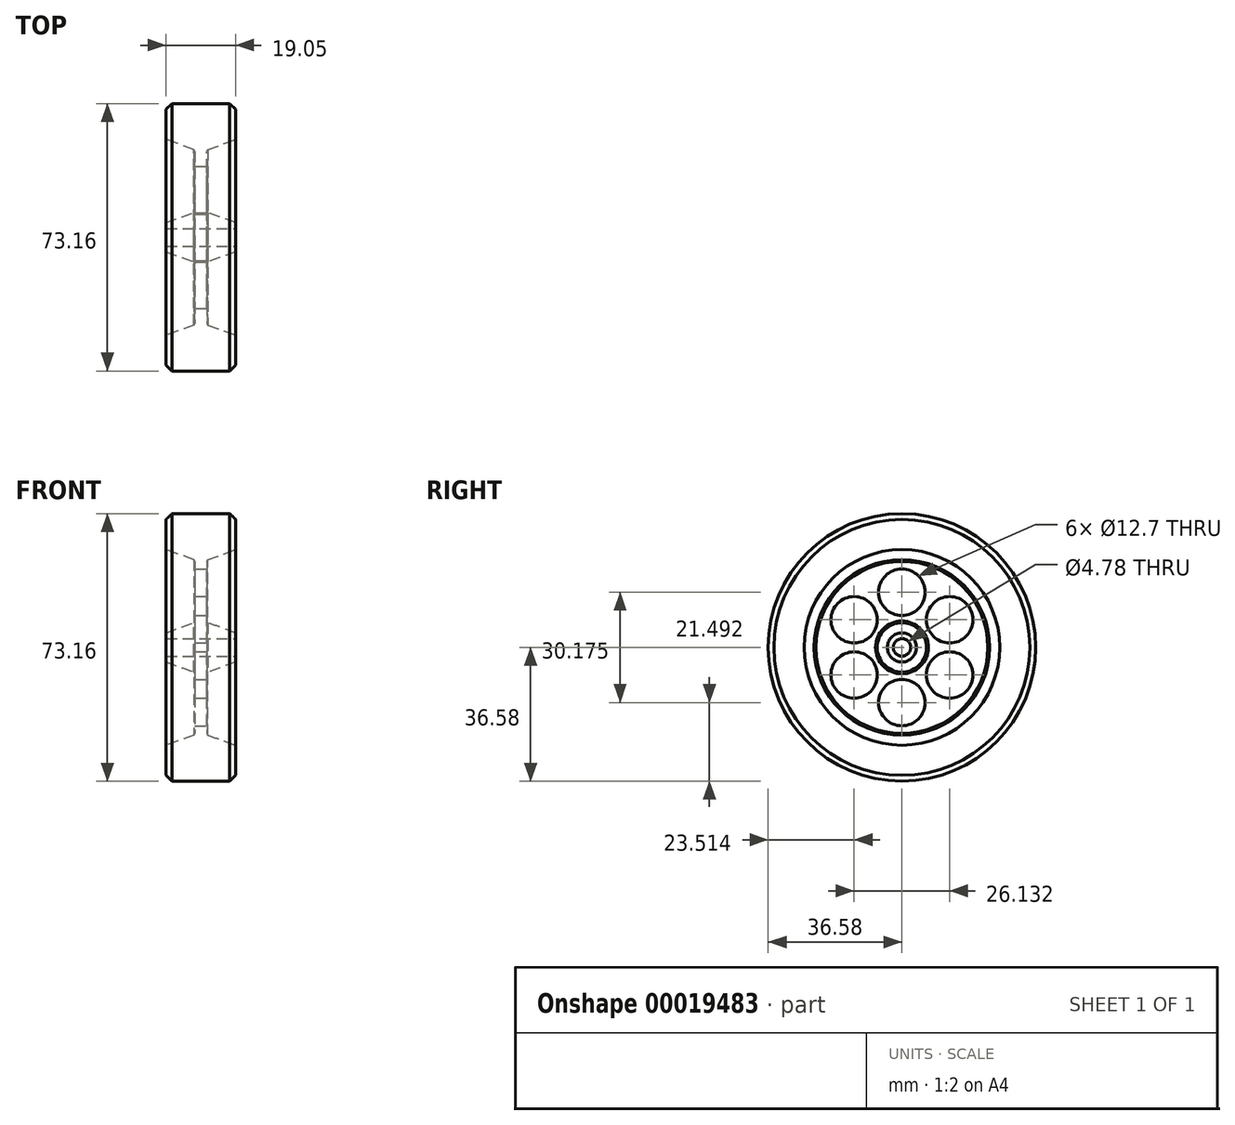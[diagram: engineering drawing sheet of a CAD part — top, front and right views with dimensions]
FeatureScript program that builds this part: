
annotation { "Feature Type Name" : "Feature", "Feature Type Description" : "" }
export const myFeature = defineFeature(function(context is Context, id is Id, definition is map)
    precondition{}
    {
        {
            var Q0;
            Q0=qCreatedBy(makeId("Front.planeOp"),FACE);
            var sketch = newSketch(context, id + "F0", { "sketchPlane" : qUnion([Q0])});
            skLineSegment(sketch, "E0", {"start": v(0, 0) * mm, "end": v(0, -3.98) * mm});
            skLineSegment(sketch, "E1", {"start": v(0, -3.98) * mm, "end": v(7.92, -6.86) * mm});
            skLineSegment(sketch, "E2", {"start": v(7.92, -6.86) * mm, "end": v(7.92, -23.88) * mm});
            skLineSegment(sketch, "E3", {"start": v(7.92, -23.88) * mm, "end": v(0, -26.76) * mm});
            skLineSegment(sketch, "E4", {"start": v(0, -26.76) * mm, "end": v(0, -36.58) * mm});
            skLineSegment(sketch, "E5", {"start": v(0, -36.58) * mm, "end": v(9.53, -36.58) * mm});
            skLineSegment(sketch, "E6", {"start": v(0, 0) * mm, "end": v(29.58, 0) * mm, "construction": true});
            skLineSegment(sketch, "E7", {"start": v(9.53, -36.58) * mm, "end": v(9.53, 2.67) * mm, "construction": true});
            skLineSegment(sketch, "E8.MirrorCS", {"start": v(11.13, -6.86) * mm, "end": v(11.13, -23.88) * mm});
            skLineSegment(sketch, "E9.MirrorCS", {"start": v(11.13, -23.88) * mm, "end": v(19.05, -26.76) * mm});
            skLineSegment(sketch, "E10.MirrorCS", {"start": v(19.05, -3.98) * mm, "end": v(11.13, -6.86) * mm});
            skLineSegment(sketch, "E11.MirrorCS", {"start": v(19.05, -26.76) * mm, "end": v(19.05, -36.58) * mm});
            skLineSegment(sketch, "E12.MirrorCS", {"start": v(19.05, -36.58) * mm, "end": v(9.53, -36.58) * mm});
            skLineSegment(sketch, "E13.MirrorCS", {"start": v(19.05, 0) * mm, "end": v(19.05, -3.98) * mm});
            skLineSegment(sketch, "E14", {"start": v(0, 0) * mm, "end": v(19.05, 0) * mm});
            skSolve(sketch);
        }
        {
            var Q0;
            Q0 = qSketchRegion(id + "F0", true);
            var Q1;
            Q1=sQuery(id+"F0.wireOp",EDGE,"E6");
            revolve(context, id + "F1", {"entities" : qUnion([Q0]), "axis" : qUnion([Q1]), "revolveType" : RevolveType.FULL});
        }
        {
            var Q0;
            Q0=makeQuery(id+"F1.opRevolve","SWEPT_FACE",FACE,{"disambiguationData":[OSD([sQuery(id+"F0.wireOp",EDGE,"E8.MirrorCS")])]});
            var sketch = newSketch(context, id + "F2", { "sketchPlane" : qUnion([Q0])});
            skCircle(sketch, "E15", {"center": v(0, 15.09) * mm, "radius": 6.35 * mm});
            skCircle(sketch, "E16.1.0", {"center": v(-13.07, 7.54) * mm, "radius": 6.35 * mm});
            skCircle(sketch, "E16.2.0", {"center": v(-13.07, -7.54) * mm, "radius": 6.35 * mm});
            skCircle(sketch, "E16.3.0", {"center": v(0, -15.09) * mm, "radius": 6.35 * mm});
            skCircle(sketch, "E16.4.0", {"center": v(13.07, -7.54) * mm, "radius": 6.35 * mm});
            skCircle(sketch, "E16.5.0", {"center": v(13.07, 7.54) * mm, "radius": 6.35 * mm});
            skPoint(sketch, "E16.center", {"position": v(0, 0) * mm});
            skSolve(sketch);
        }
        {
            var Q0;
            Q0 = qSketchRegion(id + "F2", true);
            extrude(context, id + "F3", {"entities" : qUnion([Q0]), "operationType" : NewBodyOperationType.REMOVE, "endBound" : BoundingType.THROUGH_ALL, "oppositeDirection" : true, "depth" : 25.4 * mm});
        }
        {
            var Q0;
            Q0=makeQuery(id+"F1.opRevolve","SWEPT_FACE",FACE,{"disambiguationData":[OSD([sQuery(id+"F0.wireOp",EDGE,"E13.MirrorCS")])]});
            var sketch = newSketch(context, id + "F4", { "sketchPlane" : qUnion([Q0])});
            skPoint(sketch, "E17", {"position": v(0, 0) * mm});
            skSolve(sketch);
        }
        {
            var Q0;
            Q0=sQuery(id+"F4.wireOp",VERTEX,"E17");
            var Q1;
            Q1=makeQuery(id+"F1.opRevolve","SWEPT_BODY",BODY,{"disambiguationData":[OSD([sQuery(id+"F0.wireOp",EDGE,"E0"),sQuery(id+"F0.wireOp",EDGE,"E1"),sQuery(id+"F0.wireOp",EDGE,"E2"),sQuery(id+"F0.wireOp",EDGE,"E3"),sQuery(id+"F0.wireOp",EDGE,"E4"),sQuery(id+"F0.wireOp",EDGE,"E5"),sQuery(id+"F0.wireOp",EDGE,"E8.MirrorCS"),sQuery(id+"F0.wireOp",EDGE,"E9.MirrorCS"),sQuery(id+"F0.wireOp",EDGE,"E10.MirrorCS"),sQuery(id+"F0.wireOp",EDGE,"E11.MirrorCS"),sQuery(id+"F0.wireOp",EDGE,"E12.MirrorCS"),sQuery(id+"F0.wireOp",EDGE,"E13.MirrorCS"),sQuery(id+"F0.wireOp",EDGE,"E14")])]});
            hole(context, id + "F5", {"style" : HoleStyle.SIMPLE, "holeDiameter" : 4.78 * mm, "endStyle" : HoleEndStyle.THROUGH, "locations" : qUnion([Q0]), "scope" : qUnion([Q1])});
        }
        {
            var Q0;
            Q0=makeQuery(id+"F1.opRevolve","SWEPT_EDGE",EDGE,{"disambiguationData":[OSD([sQuery(id+"F0.wireOp",EDGE,"E8.MirrorCS"),sQuery(id+"F0.wireOp",EDGE,"E10.MirrorCS")])]});
            var Q1;
            Q1=makeQuery(id+"F1.opRevolve","SWEPT_EDGE",EDGE,{"disambiguationData":[OSD([sQuery(id+"F0.wireOp",EDGE,"E8.MirrorCS"),sQuery(id+"F0.wireOp",EDGE,"E9.MirrorCS")])]});
            var Q2;
            Q2=makeQuery(id+"F1.opRevolve","SWEPT_EDGE",EDGE,{"disambiguationData":[OSD([sQuery(id+"F0.wireOp",EDGE,"E1"),sQuery(id+"F0.wireOp",EDGE,"E2")])]});
            var Q3;
            Q3=makeQuery(id+"F1.opRevolve","SWEPT_EDGE",EDGE,{"disambiguationData":[OSD([sQuery(id+"F0.wireOp",EDGE,"E2"),sQuery(id+"F0.wireOp",EDGE,"E3")])]});
            chamfer(context, id + "F6", {"entities" : qUnion([Q0, Q1, Q2, Q3]), "width" : 0.5 * mm});
        }
        {
            var Q0;
            Q0=makeQuery(id+"F1.opRevolve","SWEPT_EDGE",EDGE,{"disambiguationData":[OSD([sQuery(id+"F0.wireOp",EDGE,"E4"),sQuery(id+"F0.wireOp",EDGE,"E5")])]});
            var Q1;
            Q1=makeQuery(id+"F1.opRevolve","SWEPT_EDGE",EDGE,{"disambiguationData":[OSD([sQuery(id+"F0.wireOp",EDGE,"E11.MirrorCS"),sQuery(id+"F0.wireOp",EDGE,"E12.MirrorCS")])]});
            chamfer(context, id + "F7", {"entities" : qUnion([Q0, Q1]), "chamferType" : ChamferType.OFFSET_ANGLE, "width" : 1.6 * mm, "oppositeDirection" : false, "angle" : 45 * degree});
        }
    });
